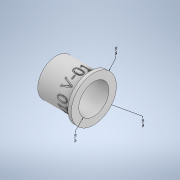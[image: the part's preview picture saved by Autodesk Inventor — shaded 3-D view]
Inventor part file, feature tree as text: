
AUTODESK INVENTOR PART (.ipt)
format: ipt  version: 2021.1 (Build 251245010, 245A)  size: 499,200 bytes
history: native  units: in
note: dims shown in document units (in); Inventor stores cm internally (conversion verified against a paired STEP export)
features: other x4, sketch x3, revolve x1, plane x1, emboss x1, helix x1
ambient origin geometry x8: Origin, YZ Plane, XZ Plane, XY Plane, X Axis, Y Axis, Z Axis, Center Point
bodies: Solid1 (feature_tree)
feature tree (11):
  other  "Annotations"
  revolve  "Revolution1"  [1 undecoded]
  plane  "Work Plane1"
  emboss  "Emboss1"
  helix  "Coil1"  [1 undecoded]
  sketch  "Sketch2"  dims[d0=0.825in d1=0.55in d2=0.125in]
  sketch  "Sketch4"  dims[d3=1.0in]
  sketch  "Sketch5"  dims[d4=90.0deg d5=0.675in d6=0.25in d10=60.0deg d11=0.0097in d12=60.0deg d13=60.0deg d15=0.1in d16=0.2in d17=0.05in d18=0.6042in d19=0.542in d20=30.0deg d21=0.1in d22=0.625in d23=0.3937in d24=0.0in d25=90.0deg d26=90.0deg d27=0.0in d28=0.0in d35=0.35in d36=0.05in d37=0.0in d29=2.0173in d30=1.65in d31=2.2078in d32=1.35in d33=1.04in d34=1.1in]
  other  "Diameter Dimension 1"
  other  "Diameter Dimension 2"
  other  "Diameter Dimension 3"
note: 2 required parameter values undecoded (feature->parameter linkage not recoverable at this tier; creation-order binding heuristic only, values carry confidence <= 0.55)